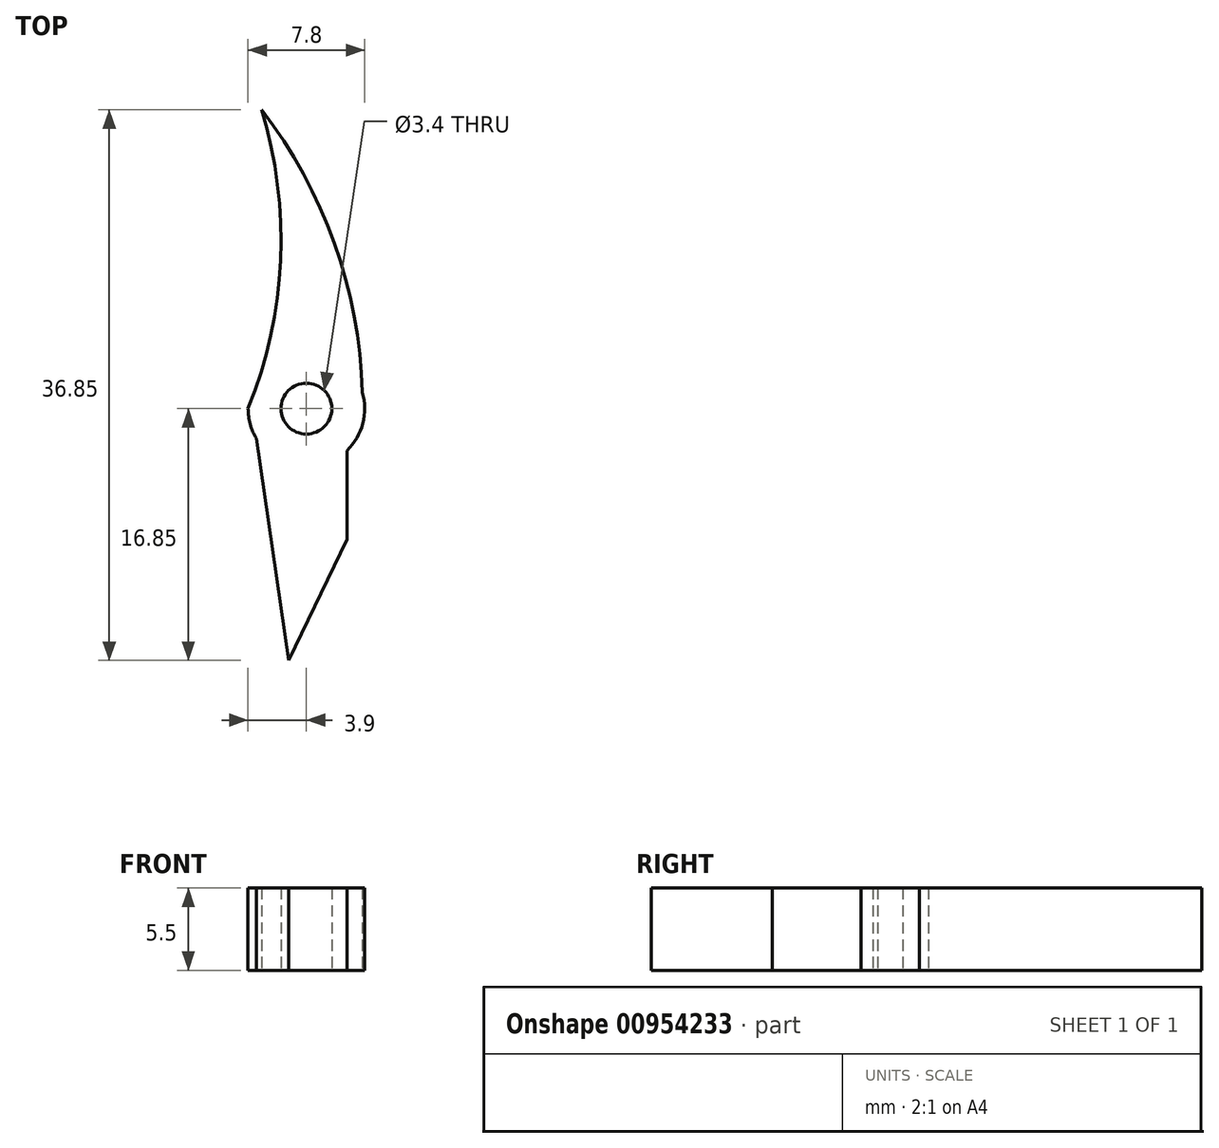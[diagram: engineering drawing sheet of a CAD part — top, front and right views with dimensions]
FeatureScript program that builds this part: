
annotation { "Feature Type Name" : "Feature", "Feature Type Description" : "" }
export const myFeature = defineFeature(function(context is Context, id is Id, definition is map)
    precondition{}
    {
        {
            var Q0;
            Q0=qCreatedBy(makeId("Top.planeOp"),FACE);
            var sketch = newSketch(context, id + "F0", { "sketchPlane" : qUnion([Q0])});
            skCircle(sketch, "E0", {"center": v(0, 0) * mm, "radius": 1.7 * mm});
            skCircle(sketch, "E1", {"center": v(0, 0) * mm, "radius": 3.9 * mm});
            skArc(sketch, "E2", {"start": v(3.74, 1.1) * mm, "mid": v(1.87, 11.08) * mm, "end": v(-3, 20) * mm});
            skArc(sketch, "E3", {"start": v(-3.9, 0) * mm, "mid": v(-1.73, 9.92) * mm, "end": v(-3, 20) * mm});
            skLineSegment(sketch, "E4", {"start": v(2.71, -2.8) * mm, "end": v(2.71, -8.74) * mm});
            skLineSegment(sketch, "E5", {"start": v(2.71, -8.74) * mm, "end": v(-1.2, -16.85) * mm});
            skLineSegment(sketch, "E6", {"start": v(-1.2, -16.85) * mm, "end": v(-3.35, -2) * mm});
            skSolve(sketch);
        }
        {
            var Q0;
            {var subQ0=sQuery(id+"F0.wireOp",EDGE,"E2");Q0=makeQuery(id+"F0.imprint","IMPRINT",FACE,{"disambiguationData":[TD([[makeQuery(id+"F0.imprint","IMPRINT",EDGE,{"derivedFrom":subQ0}),1.0]])]});}
            var Q1;
            Q1=makeQuery(id+"F0.imprint","IMPRINT",FACE,{"disambiguationData":[TD([[makeQuery(id+"F0.imprint","IMPRINT",EDGE,{"derivedFrom":sQuery(id+"F0.wireOp",EDGE,"E0")}),-1.0]])]});
            var Q2;
            {var subQ0=sQuery(id+"F0.wireOp",EDGE,"E4");Q2=makeQuery(id+"F0.imprint","IMPRINT",FACE,{"disambiguationData":[TD([[makeQuery(id+"F0.imprint","IMPRINT",EDGE,{"derivedFrom":subQ0}),-1.0]])]});}
            extrude(context, id + "F1", {"entities" : qUnion([Q0, Q1, Q2]), "depth" : 5.5 * mm, "offsetDistance" : 25 * mm});
        }
    });
